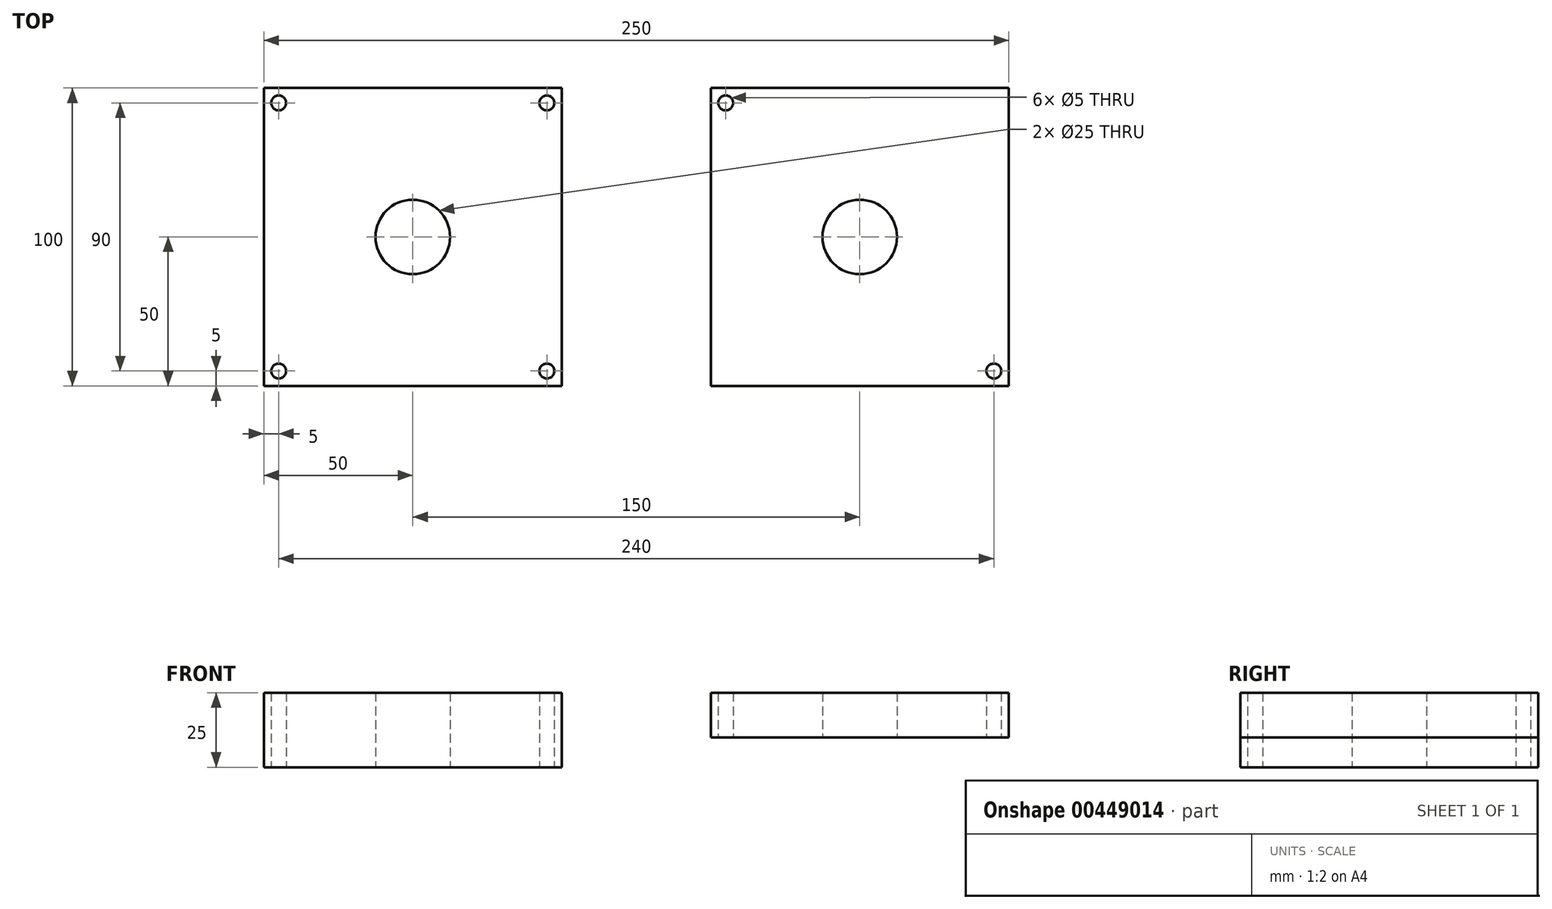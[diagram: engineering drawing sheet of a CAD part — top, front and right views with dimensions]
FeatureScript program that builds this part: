
annotation { "Feature Type Name" : "Feature", "Feature Type Description" : "" }
export const myFeature = defineFeature(function(context is Context, id is Id, definition is map)
    precondition{}
    {
        {
            var Q0;
            Q0=qCreatedBy(makeId("Top.planeOp"),FACE);
            var sketch = newSketch(context, id + "F0", { "sketchPlane" : qUnion([Q0])});
            skLineSegment(sketch, "E0.bottom", {"start": v(-50, 50) * mm, "end": v(50, 50) * mm});
            skLineSegment(sketch, "E0.top", {"start": v(-50, -50) * mm, "end": v(50, -50) * mm});
            skLineSegment(sketch, "E0.left", {"start": v(-50, 50) * mm, "end": v(-50, -50) * mm});
            skLineSegment(sketch, "E0.right", {"start": v(50, 50) * mm, "end": v(50, -50) * mm});
            skPoint(sketch, "E0.middle", {"position": v(0, 0) * mm});
            skLineSegment(sketch, "E1", {"start": v(-50, 0) * mm, "end": v(50, 0) * mm, "construction": true});
            skLineSegment(sketch, "E2", {"start": v(0, -50) * mm, "end": v(0, 50) * mm, "construction": true});
            skCircle(sketch, "E3", {"center": v(-45, -45) * mm, "radius": 2.5 * mm});
            skCircle(sketch, "E4.MirrorC", {"center": v(-45, 45) * mm, "radius": 2.5 * mm});
            skCircle(sketch, "E5.MirrorC", {"center": v(45, 45) * mm, "radius": 2.5 * mm});
            skCircle(sketch, "E6.MirrorC", {"center": v(45, -45) * mm, "radius": 2.5 * mm});
            skCircle(sketch, "E7", {"center": v(0, 0) * mm, "radius": 12.5 * mm});
            skSolve(sketch);
        }
        {
            var Q0;
            Q0=qCreatedBy(makeId("Top.planeOp"),FACE);
            var sketch = newSketch(context, id + "F1", { "sketchPlane" : qUnion([Q0])});
            skLineSegment(sketch, "E8.bottom", {"start": v(100, 50) * mm, "end": v(200, 50) * mm});
            skLineSegment(sketch, "E8.top", {"start": v(100, -50) * mm, "end": v(200, -50) * mm});
            skLineSegment(sketch, "E8.left", {"start": v(100, 50) * mm, "end": v(100, -50) * mm});
            skLineSegment(sketch, "E8.right", {"start": v(200, 50) * mm, "end": v(200, -50) * mm});
            skPoint(sketch, "E8.middle", {"position": v(150, 0) * mm});
            skLineSegment(sketch, "E9", {"start": v(100, 0) * mm, "end": v(200, 0) * mm, "construction": true});
            skLineSegment(sketch, "E10", {"start": v(150, -50) * mm, "end": v(150, 50) * mm, "construction": true});
            skCircle(sketch, "E11", {"center": v(105, -45) * mm, "radius": 2.5 * mm});
            skCircle(sketch, "E12.MirrorC", {"center": v(105, 45) * mm, "radius": 2.5 * mm});
            skCircle(sketch, "E13.MirrorC", {"center": v(195, 45) * mm, "radius": 2.5 * mm});
            skCircle(sketch, "E14.MirrorC", {"center": v(195, -45) * mm, "radius": 2.5 * mm});
            skCircle(sketch, "E15", {"center": v(150, 0) * mm, "radius": 12.5 * mm});
            skSolve(sketch);
        }
        {
            var Q0;
            Q0=qCreatedBy(makeId("Top.planeOp"),FACE);
            var sketch = newSketch(context, id + "F2", { "sketchPlane" : qUnion([Q0])});
            skLineSegment(sketch, "E16.bottom", {"start": v(253.24, 50) * mm, "end": v(353.24, 50) * mm});
            skLineSegment(sketch, "E16.top", {"start": v(253.24, -50) * mm, "end": v(353.24, -50) * mm});
            skLineSegment(sketch, "E16.left", {"start": v(253.24, 50) * mm, "end": v(253.24, -50) * mm});
            skLineSegment(sketch, "E16.right", {"start": v(353.24, 50) * mm, "end": v(353.24, -50) * mm});
            skPoint(sketch, "E16.middle", {"position": v(303.24, 0) * mm});
            skLineSegment(sketch, "E17", {"start": v(253.24, 0) * mm, "end": v(353.24, 0) * mm, "construction": true});
            skLineSegment(sketch, "E18", {"start": v(303.24, -50) * mm, "end": v(303.24, 50) * mm, "construction": true});
            skCircle(sketch, "E19", {"center": v(258.24, -45) * mm, "radius": 2.5 * mm});
            skCircle(sketch, "E20.MirrorC", {"center": v(258.24, 45) * mm, "radius": 2.5 * mm});
            skCircle(sketch, "E21.MirrorC", {"center": v(348.24, 45) * mm, "radius": 2.5 * mm});
            skCircle(sketch, "E22.MirrorC", {"center": v(348.24, -45) * mm, "radius": 2.5 * mm});
            skCircle(sketch, "E23", {"center": v(303.24, 0) * mm, "radius": 12.5 * mm});
            skSolve(sketch);
        }
        {
            var Q0;
            Q0=makeQuery(id+"F1.imprint","IMPRINT",FACE,{"disambiguationData":[TD([[makeQuery(id+"F1.imprint","IMPRINT",EDGE,{"derivedFrom":sQuery(id+"F1.wireOp",EDGE,"E8.bottom")}),-1.0]])]});
            var Q1;
            Q1=makeQuery(id+"F1.imprint","IMPRINT",FACE,{"disambiguationData":[TD([[makeQuery(id+"F1.imprint","IMPRINT",EDGE,{"derivedFrom":sQuery(id+"F1.wireOp",EDGE,"E15")}),1.0]])]});
            var Q2;
            Q2=makeQuery(id+"F1.imprint","IMPRINT",FACE,{"disambiguationData":[TD([[makeQuery(id+"F1.imprint","IMPRINT",EDGE,{"derivedFrom":sQuery(id+"F1.wireOp",EDGE,"E14.MirrorC")}),-1.0]])]});
            var Q3;
            Q3=makeQuery(id+"F1.imprint","IMPRINT",FACE,{"disambiguationData":[TD([[makeQuery(id+"F1.imprint","IMPRINT",EDGE,{"derivedFrom":sQuery(id+"F1.wireOp",EDGE,"E13.MirrorC")}),1.0]])]});
            var Q4;
            Q4=makeQuery(id+"F1.imprint","IMPRINT",FACE,{"disambiguationData":[TD([[makeQuery(id+"F1.imprint","IMPRINT",EDGE,{"derivedFrom":sQuery(id+"F1.wireOp",EDGE,"E12.MirrorC")}),-1.0]])]});
            var Q5;
            Q5=makeQuery(id+"F1.imprint","IMPRINT",FACE,{"disambiguationData":[TD([[makeQuery(id+"F1.imprint","IMPRINT",EDGE,{"derivedFrom":sQuery(id+"F1.wireOp",EDGE,"E11")}),1.0]])]});
            extrude(context, id + "F3", {"entities" : qUnion([Q0, Q1, Q2, Q3, Q4, Q5]), "depth" : 25 * mm});
        }
        {
            var Q0;
            Q0=makeQuery(id+"F2.imprint","IMPRINT",FACE,{"disambiguationData":[TD([[makeQuery(id+"F2.imprint","IMPRINT",EDGE,{"derivedFrom":sQuery(id+"F2.wireOp",EDGE,"E23")}),1.0]])]});
            var Q1;
            Q1=makeQuery(id+"F2.imprint","IMPRINT",FACE,{"disambiguationData":[TD([[makeQuery(id+"F2.imprint","IMPRINT",EDGE,{"derivedFrom":sQuery(id+"F2.wireOp",EDGE,"E16.bottom")}),-1.0]])]});
            var Q2;
            Q2=makeQuery(id+"F2.imprint","IMPRINT",FACE,{"disambiguationData":[TD([[makeQuery(id+"F2.imprint","IMPRINT",EDGE,{"derivedFrom":sQuery(id+"F2.wireOp",EDGE,"E21.MirrorC")}),1.0]])]});
            var Q3;
            Q3=makeQuery(id+"F2.imprint","IMPRINT",FACE,{"disambiguationData":[TD([[makeQuery(id+"F2.imprint","IMPRINT",EDGE,{"derivedFrom":sQuery(id+"F2.wireOp",EDGE,"E22.MirrorC")}),-1.0]])]});
            var Q4;
            Q4=makeQuery(id+"F2.imprint","IMPRINT",FACE,{"disambiguationData":[TD([[makeQuery(id+"F2.imprint","IMPRINT",EDGE,{"derivedFrom":sQuery(id+"F2.wireOp",EDGE,"E19")}),1.0]])]});
            var Q5;
            Q5=makeQuery(id+"F2.imprint","IMPRINT",FACE,{"disambiguationData":[TD([[makeQuery(id+"F2.imprint","IMPRINT",EDGE,{"derivedFrom":sQuery(id+"F2.wireOp",EDGE,"E20.MirrorC")}),-1.0]])]});
            extrude(context, id + "F4", {"entities" : qUnion([Q0, Q1, Q2, Q3, Q4, Q5]), "depth" : 12.5 * mm});
        }
        {
            var Q0;
            Q0=makeQuery(id+"F4.opExtrude","CAP_FACE",FACE,{"disambiguationData":[OSD([sQuery(id+"F2.wireOp",EDGE,"E16.bottom"),sQuery(id+"F2.wireOp",EDGE,"E16.top"),sQuery(id+"F2.wireOp",EDGE,"E16.left"),sQuery(id+"F2.wireOp",EDGE,"E16.right")])],"isStart":false});
            extrude(context, id + "F5", {"entities" : qUnion([Q0]), "depth" : 12.5 * mm});
        }
        {
            var Q0;
            Q0 = qSketchRegion(id + "F0", true);
            extrude(context, id + "F6", {"entities" : qUnion([Q0]), "depth" : 25 * mm});
        }
        {
            var Q0;
            Q0=makeQuery(id+"F1.imprint","IMPRINT",FACE,{"disambiguationData":[TD([[makeQuery(id+"F1.imprint","IMPRINT",EDGE,{"derivedFrom":sQuery(id+"F1.wireOp",EDGE,"E15")}),1.0]])]});
            extrude(context, id + "F7", {"entities" : qUnion([Q0]), "operationType" : NewBodyOperationType.REMOVE, "endBound" : BoundingType.THROUGH_ALL, "depth" : 25 * mm});
        }
        {
            var Q0;
            Q0=makeQuery(id+"F1.imprint","IMPRINT",FACE,{"disambiguationData":[TD([[makeQuery(id+"F1.imprint","IMPRINT",EDGE,{"derivedFrom":sQuery(id+"F1.wireOp",EDGE,"E14.MirrorC")}),-1.0]])]});
            var Q1;
            Q1=makeQuery(id+"F1.imprint","IMPRINT",FACE,{"disambiguationData":[TD([[makeQuery(id+"F1.imprint","IMPRINT",EDGE,{"derivedFrom":sQuery(id+"F1.wireOp",EDGE,"E11")}),1.0]])]});
            var Q2;
            Q2=makeQuery(id+"F1.imprint","IMPRINT",FACE,{"disambiguationData":[TD([[makeQuery(id+"F1.imprint","IMPRINT",EDGE,{"derivedFrom":sQuery(id+"F1.wireOp",EDGE,"E12.MirrorC")}),-1.0]])]});
            var Q3;
            Q3=makeQuery(id+"F1.imprint","IMPRINT",FACE,{"disambiguationData":[TD([[makeQuery(id+"F1.imprint","IMPRINT",EDGE,{"derivedFrom":sQuery(id+"F1.wireOp",EDGE,"E13.MirrorC")}),1.0]])]});
            extrude(context, id + "F8", {"entities" : qUnion([Q0, Q1, Q2, Q3]), "operationType" : NewBodyOperationType.REMOVE, "depth" : 10 * mm});
        }
        {
            var Q0;
            Q0=makeQuery(id+"F2.imprint","IMPRINT",FACE,{"disambiguationData":[TD([[makeQuery(id+"F2.imprint","IMPRINT",EDGE,{"derivedFrom":sQuery(id+"F2.wireOp",EDGE,"E23")}),1.0]])]});
            var Q1;
            Q1=makeQuery(id+"F2.imprint","IMPRINT",FACE,{"disambiguationData":[TD([[makeQuery(id+"F2.imprint","IMPRINT",EDGE,{"derivedFrom":sQuery(id+"F2.wireOp",EDGE,"E22.MirrorC")}),-1.0]])]});
            var Q2;
            Q2=makeQuery(id+"F2.imprint","IMPRINT",FACE,{"disambiguationData":[TD([[makeQuery(id+"F2.imprint","IMPRINT",EDGE,{"derivedFrom":sQuery(id+"F2.wireOp",EDGE,"E19")}),1.0]])]});
            var Q3;
            Q3=makeQuery(id+"F2.imprint","IMPRINT",FACE,{"disambiguationData":[TD([[makeQuery(id+"F2.imprint","IMPRINT",EDGE,{"derivedFrom":sQuery(id+"F2.wireOp",EDGE,"E20.MirrorC")}),-1.0]])]});
            var Q4;
            Q4=makeQuery(id+"F2.imprint","IMPRINT",FACE,{"disambiguationData":[TD([[makeQuery(id+"F2.imprint","IMPRINT",EDGE,{"derivedFrom":sQuery(id+"F2.wireOp",EDGE,"E21.MirrorC")}),1.0]])]});
            extrude(context, id + "F9", {"entities" : qUnion([Q0, Q1, Q2, Q3, Q4]), "operationType" : NewBodyOperationType.REMOVE, "endBound" : BoundingType.THROUGH_ALL, "depth" : 25 * mm});
        }
    });
